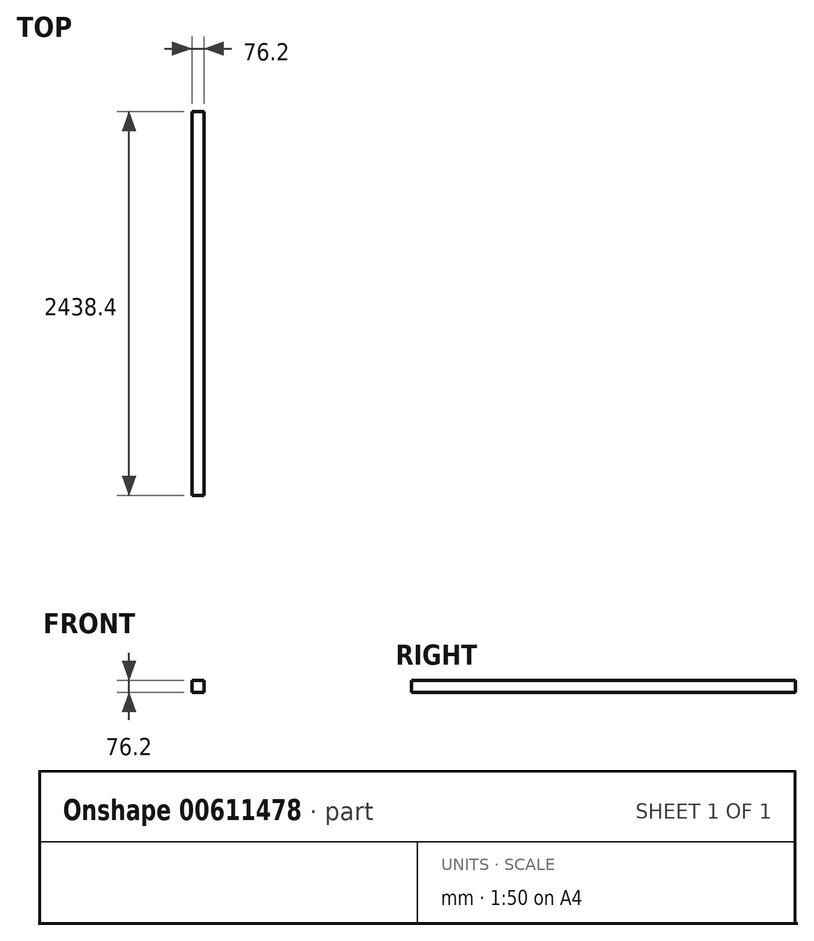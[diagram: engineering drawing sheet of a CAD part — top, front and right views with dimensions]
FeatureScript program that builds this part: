
annotation { "Feature Type Name" : "Feature", "Feature Type Description" : "" }
export const myFeature = defineFeature(function(context is Context, id is Id, definition is map)
    precondition{}
    {
        {
            var Q0;
            Q0=qCreatedBy(makeId("Front.planeOp"),FACE);
            var sketch = newSketch(context, id + "F0", { "sketchPlane" : qUnion([Q0])});
            skLineSegment(sketch, "E0.bottom", {"start": v(0, 0) * mm, "end": v(76.2, 0) * mm});
            skLineSegment(sketch, "E0.top", {"start": v(0, -76.2) * mm, "end": v(76.2, -76.2) * mm});
            skLineSegment(sketch, "E0.left", {"start": v(0, 0) * mm, "end": v(0, -76.2) * mm});
            skLineSegment(sketch, "E0.right", {"start": v(76.2, 0) * mm, "end": v(76.2, -76.2) * mm});
            skSolve(sketch);
        }
        {
            var Q0;
            Q0=makeQuery(id+"F0.imprint","IMPRINT",FACE,{"disambiguationData":[TD([[makeQuery(id+"F0.imprint","IMPRINT",EDGE,{"derivedFrom":sQuery(id+"F0.wireOp",EDGE,"E0.bottom")}),-1.0]])]});
            extrude(context, id + "F1", {"entities" : qUnion([Q0]), "depth" : 2438.4 * mm, "offsetDistance" : 25.4 * mm});
        }
    });
